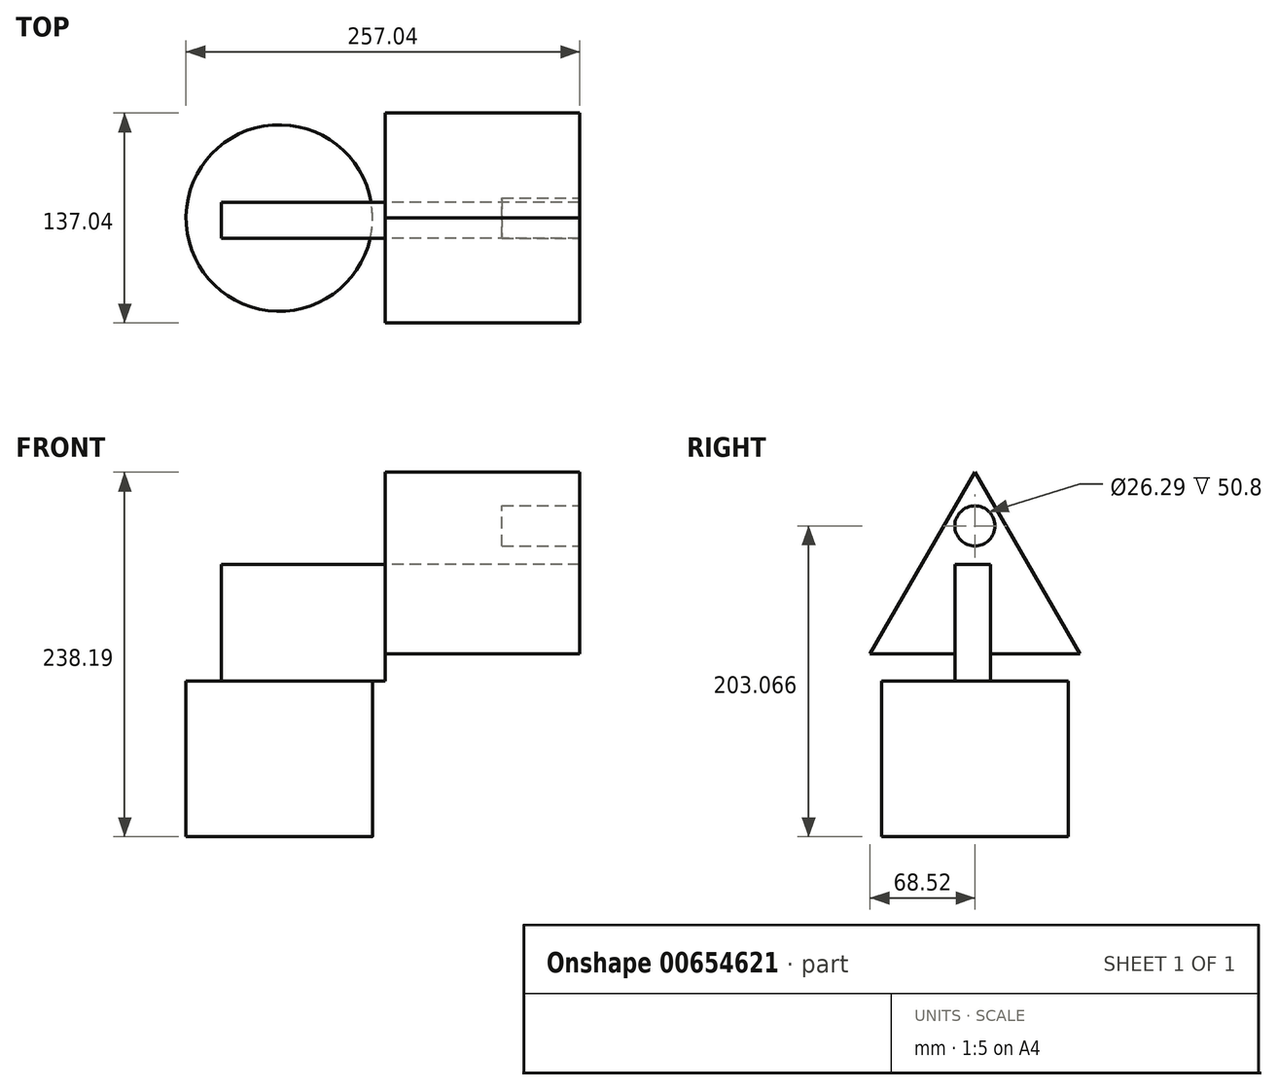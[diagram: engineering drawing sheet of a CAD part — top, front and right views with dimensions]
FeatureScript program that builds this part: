
annotation { "Feature Type Name" : "Feature", "Feature Type Description" : "" }
export const myFeature = defineFeature(function(context is Context, id is Id, definition is map)
    precondition{}
    {
        {
            var Q0;
            Q0=qCreatedBy(makeId("Top.planeOp"),FACE);
            var sketch = newSketch(context, id + "F0", { "sketchPlane" : qUnion([Q0])});
            skCircle(sketch, "E0", {"center": v(0, 0) * mm, "radius": 60.88 * mm});
            skSolve(sketch);
        }
        {
            var Q0;
            Q0=makeQuery(id+"F0.imprint","IMPRINT",FACE,{"disambiguationData":[TD([[makeQuery(id+"F0.imprint","IMPRINT",EDGE,{"derivedFrom":sQuery(id+"F0.wireOp",EDGE,"E0")}),1.0]])]});
            extrude(context, id + "F1", {"entities" : qUnion([Q0]), "depth" : 101.6 * mm, "offsetDistance" : 25.4 * mm});
        }
        {
            var Q0;
            Q0=makeQuery(id+"F1.opExtrude","CAP_FACE",FACE,{"disambiguationData":[OSD([sQuery(id+"F0.wireOp",EDGE,"E0")])],"isStart":false});
            var sketch = newSketch(context, id + "F2", { "sketchPlane" : qUnion([Q0])});
            skLineSegment(sketch, "E1.bottom", {"start": v(-37.97, 10.25) * mm, "end": v(43.76, 10.25) * mm});
            skLineSegment(sketch, "E1.top", {"start": v(-37.97, -13.14) * mm, "end": v(43.76, -13.14) * mm});
            skLineSegment(sketch, "E1.left", {"start": v(-37.97, 10.25) * mm, "end": v(-37.97, -13.14) * mm});
            skLineSegment(sketch, "E1.right", {"start": v(43.76, 10.25) * mm, "end": v(43.76, -13.14) * mm});
            skSolve(sketch);
        }
        {
            var Q0;
            Q0=makeQuery(id+"F2.imprint","IMPRINT",FACE,{"disambiguationData":[TD([[makeQuery(id+"F2.imprint","IMPRINT",EDGE,{"derivedFrom":sQuery(id+"F2.wireOp",EDGE,"E1.bottom")}),-1.0]])]});
            extrude(context, id + "F3", {"entities" : qUnion([Q0]), "operationType" : NewBodyOperationType.ADD, "depth" : 76.2 * mm, "offsetDistance" : 25.4 * mm});
        }
        {
            var Q0;
            Q0=makeQuery(id+"F3.opExtrude","SWEPT_FACE",FACE,{"disambiguationData":[OSD([sQuery(id+"F2.wireOp",EDGE,"E1.right")])]});
            extrude(context, id + "F4", {"entities" : qUnion([Q0]), "operationType" : NewBodyOperationType.ADD, "depth" : 25.4 * mm, "offsetDistance" : 25.4 * mm});
        }
        {
            var Q0;
            Q0=makeQuery(id+"F4.opExtrude","CAP_FACE",FACE,{"disambiguationData":[OSD([sQuery(id+"F2.wireOp",EDGE,"E1.right")])],"isStart":false});
            var sketch = newSketch(context, id + "F5", { "sketchPlane" : qUnion([Q0])});
            skCircle(sketch, "E2.cCircle", {"center": v(0, 159.07) * mm, "radius": 39.56 * mm, "construction": true});
            skLineSegment(sketch, "E2.0", {"start": v(68.52, 119.5) * mm, "end": v(-68.52, 119.5) * mm});
            skLineSegment(sketch, "E2.1", {"start": v(-68.52, 119.5) * mm, "end": v(0, 238.19) * mm});
            skLineSegment(sketch, "E2.2", {"start": v(0, 238.19) * mm, "end": v(68.52, 119.5) * mm});
            skPoint(sketch, "E2.0.midPoint", {"position": v(0, 119.5) * mm});
            skSolve(sketch);
        }
        {
            var Q0;
            {var subQ1=sQuery(id+"F5.wireOp",EDGE,"E2.1");Q0=makeQuery(id+"F5.imprint","IMPRINT",FACE,{"disambiguationData":[TD([[makeQuery(id+"F5.imprint","IMPRINT",EDGE,{"derivedFrom":subQ1}),-1.0]])]});}
            extrude(context, id + "F6", {"entities" : qUnion([Q0]), "depth" : 101.6 * mm, "offsetDistance" : 25.4 * mm});
        }
        {
            var Q0;
            Q0=makeQuery(id+"F6.opExtrude","CAP_FACE",FACE,{"disambiguationData":[OSD([sQuery(id+"F2.wireOp",EDGE,"E1.bottom"),sQuery(id+"F2.wireOp",EDGE,"E1.top"),sQuery(id+"F2.wireOp",EDGE,"E1.right"),sQuery(id+"F5.wireOp",EDGE,"E2.0"),sQuery(id+"F5.wireOp",EDGE,"E2.1"),sQuery(id+"F5.wireOp",EDGE,"E2.2")])],"isStart":false});
            extrude(context, id + "F7", {"entities" : qUnion([Q0]), "operationType" : NewBodyOperationType.ADD, "depth" : 25.4 * mm, "offsetDistance" : 25.4 * mm});
        }
        {
            var Q0;
            Q0=makeQuery(id+"F7.opExtrude","CAP_FACE",FACE,{"disambiguationData":[OSD([sQuery(id+"F2.wireOp",EDGE,"E1.bottom"),sQuery(id+"F2.wireOp",EDGE,"E1.top"),sQuery(id+"F2.wireOp",EDGE,"E1.right"),sQuery(id+"F5.wireOp",EDGE,"E2.0"),sQuery(id+"F5.wireOp",EDGE,"E2.1"),sQuery(id+"F5.wireOp",EDGE,"E2.2")])],"isStart":false});
            var sketch = newSketch(context, id + "F8", { "sketchPlane" : qUnion([Q0])});
            skCircle(sketch, "E3", {"center": v(0, 203.07) * mm, "radius": 13.14 * mm});
            skSolve(sketch);
        }
        {
            var Q0;
            Q0=makeQuery(id+"F8.imprint","IMPRINT",FACE,{"disambiguationData":[TD([[makeQuery(id+"F8.imprint","IMPRINT",EDGE,{"derivedFrom":sQuery(id+"F8.wireOp",EDGE,"E3")}),1.0]])]});
            extrude(context, id + "F9", {"entities" : qUnion([Q0]), "operationType" : NewBodyOperationType.REMOVE, "oppositeDirection" : true, "depth" : 50.8 * mm, "offsetDistance" : 25.4 * mm});
        }
    });
